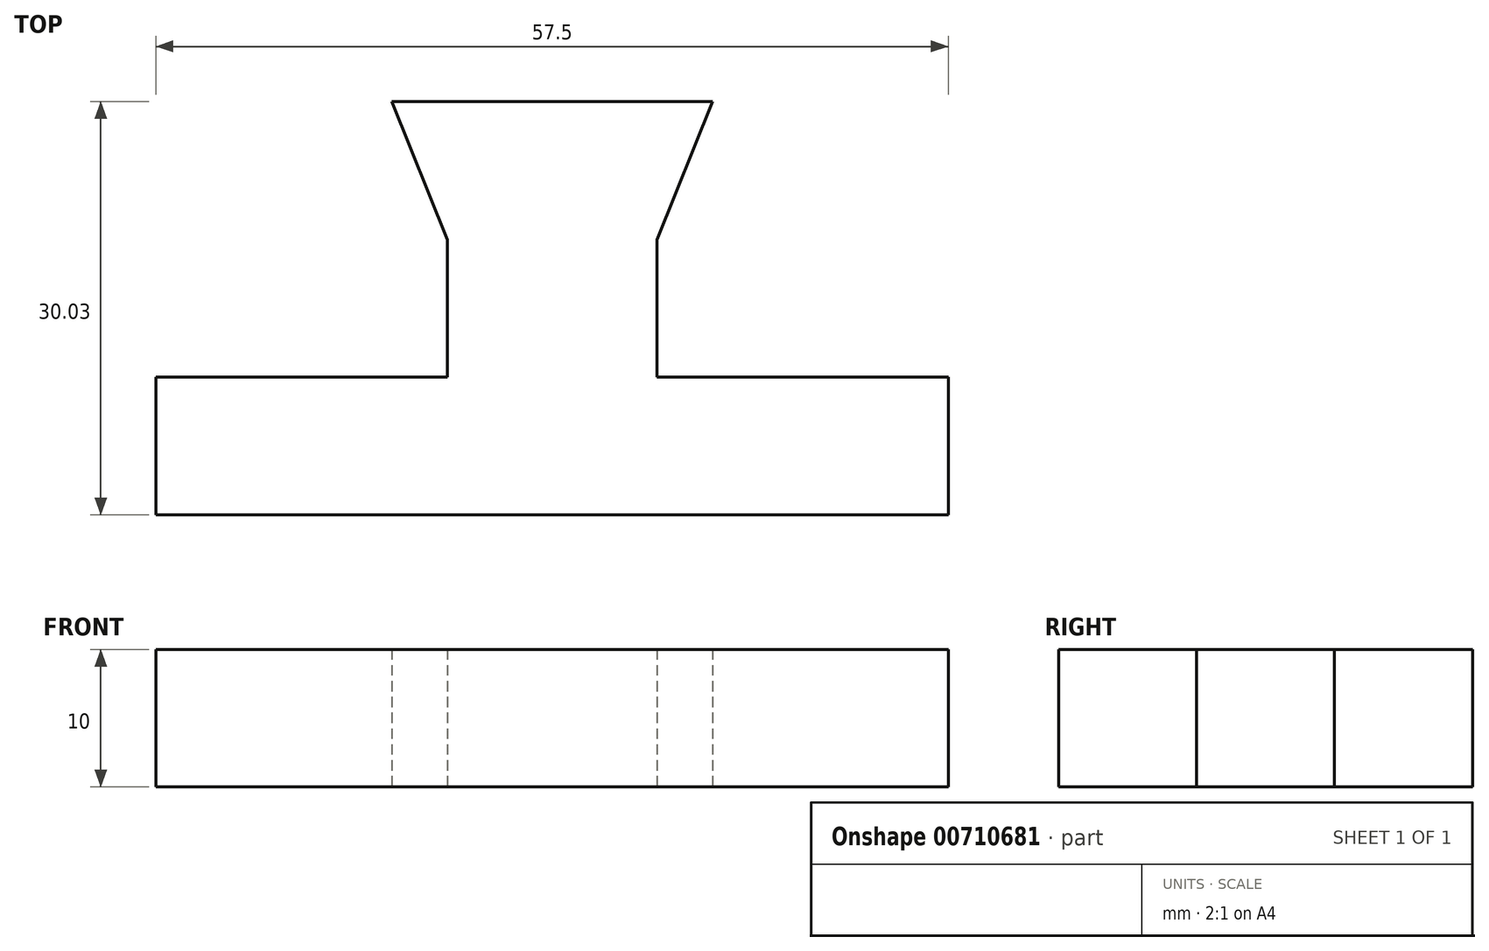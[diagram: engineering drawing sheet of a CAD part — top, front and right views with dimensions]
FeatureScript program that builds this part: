
annotation { "Feature Type Name" : "Feature", "Feature Type Description" : "" }
export const myFeature = defineFeature(function(context is Context, id is Id, definition is map)
    precondition{}
    {
        {
            var Q0;
            Q0=qCreatedBy(makeId("Top.planeOp"),FACE);
            var sketch = newSketch(context, id + "F0", { "sketchPlane" : qUnion([Q0])});
            skLineSegment(sketch, "E0", {"start": v(-7.6, 10) * mm, "end": v(-7.6, 0) * mm});
            skLineSegment(sketch, "E1", {"start": v(-7.6, 0) * mm, "end": v(-28.75, 0) * mm});
            skLineSegment(sketch, "E2", {"start": v(-28.75, 0) * mm, "end": v(-28.75, -10) * mm});
            skLineSegment(sketch, "E3", {"start": v(-28.75, -10) * mm, "end": v(28.75, -10) * mm});
            skLineSegment(sketch, "E4", {"start": v(28.75, -10) * mm, "end": v(28.75, 0) * mm});
            skLineSegment(sketch, "E5", {"start": v(28.75, 0) * mm, "end": v(7.6, 0) * mm});
            skLineSegment(sketch, "E6", {"start": v(7.6, 0) * mm, "end": v(7.6, 10) * mm});
            skLineSegment(sketch, "E7", {"start": v(-7.6, 10) * mm, "end": v(-11.64, 20.03) * mm});
            skLineSegment(sketch, "E8.MirrorCS", {"start": v(7.6, 10) * mm, "end": v(7.6, 0) * mm});
            skLineSegment(sketch, "E9.MirrorCS", {"start": v(7.6, 10) * mm, "end": v(11.64, 20.03) * mm});
            skLineSegment(sketch, "E10", {"start": v(-11.64, 20.03) * mm, "end": v(11.64, 20.03) * mm});
            skSolve(sketch);
        }
        {
            var Q0;
            Q0 = qSketchRegion(id + "F0", true);
            extrude(context, id + "F1", {"entities" : qUnion([Q0]), "depth" : 10 * mm, "offsetDistance" : 25 * mm});
        }
    });
